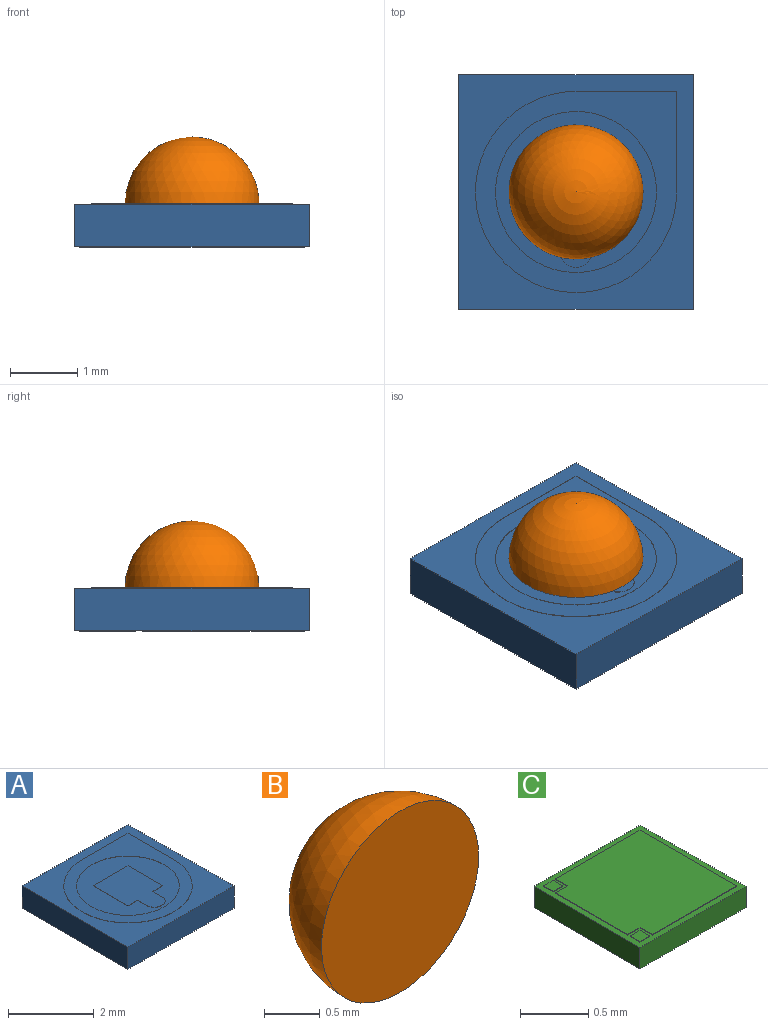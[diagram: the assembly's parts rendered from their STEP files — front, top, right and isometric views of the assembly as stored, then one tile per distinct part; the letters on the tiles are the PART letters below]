
ASSEMBLY  parts=3 mates=1
PART A: 31 faces, bbox 3.5x3.5x0.6 mm
  f0: plane 3.5x3.5mm, normal (0,0,-1), area 1.4mm2, adj f2,f3,f4,f5,f21,f22,f23,f24
  f1: plane 3.5x3.5mm, normal (0,0,1), area 4.7mm2, adj f2,f3,f4,f5,f6,f7,f9
  f2: plane 3.5x0.64mm, normal (0,-1,0), area 2.2mm2, adj f0,f1,f3,f5
  f3: plane 3.5x0.64mm, normal (1,0,0), area 2.2mm2, adj f0,f1,f2,f4
  f4: plane 3.5x0.64mm, normal (0,1,0), area 2.2mm2, adj f0,f1,f3,f5
  f5: plane 3.5x0.64mm, normal (-1,0,0), area 2.2mm2, adj f0,f1,f2,f4
  f6: plane 1.5x0.01mm, normal (1,0,0), area 0mm2, adj f1,f7,f9,f10
  f7: plane 1.5x0.01mm, normal (0,1,0), area 0mm2, adj f1,f6,f9,f10
  f8: cylinder r=1.2mm len=2.4mm, axis (0,0,-1), area 0mm2, adj f10,f11
  f9: cylinder r=1.5mm len=3mm, axis (0,0,-1), area 0mm2, adj f1,f6,f7,f10
  f10: plane 3x3mm, normal (0,0,1), area 3mm2, adj f6,f7,f8,f9
  f11: plane 2.4x2.4mm, normal (0,0,1), area 3mm2, adj f8,f12,f13,f14,f15,f16,f17,f18
  f12: plane 0.32x0.01mm, normal (0,-1,0), area 0mm2, adj f11,f13,f19,f20
  f13: plane 1.14x0.01mm, normal (1,0,0), area 0mm2, adj f11,f12,f14,f20
  f14: plane 1.14x0.01mm, normal (0,1,0), area 0mm2, adj f11,f13,f15,f20
  f15: plane 1.14x0.01mm, normal (-1,0,0), area 0mm2, adj f11,f14,f16,f20
  f16: plane 0.32x0.01mm, normal (0,-1,0), area 0mm2, adj f11,f15,f17,f20
  f17: plane 0.3x0.01mm, normal (-1,0,0), area 0mm2, adj f11,f16,f18,f20
  f18: cylinder r=0.25mm len=0.5mm, axis (0,0,-1), area 0mm2, adj f11,f17,f19,f20
  f19: plane 0.3x0.01mm, normal (1,0,0), area 0mm2, adj f11,f12,f18,f20
  f20: plane 1.69x1.14mm, normal (0,0,1), area 1.6mm2, adj f12,f13,f14,f15,f16,f17,f18,f19
  f21: plane 3.35x0.01mm, normal (0,-1,0), area 0mm2, adj f0,f22,f24,f25
  f22: plane 2.41x0.01mm, normal (-1,0,0), area 0mm2, adj f0,f21,f23,f25
  f23: plane 3.35x0.01mm, normal (0,1,0), area 0mm2, adj f0,f22,f24,f25
  f24: plane 2.41x0.01mm, normal (1,0,0), area 0mm2, adj f0,f21,f23,f25
  f25: plane 3.35x2.41mm, normal (0,0,-1), area 8.1mm2, adj f21,f22,f23,f24
  f26: plane 3.35x0.01mm, normal (0,1,0), area 0mm2, adj f0,f27,f29,f30
  f27: plane 0.84x0.01mm, normal (1,0,0), area 0mm2, adj f0,f26,f28,f30
  f28: plane 3.35x0.01mm, normal (0,-1,0), area 0mm2, adj f0,f27,f29,f30
  f29: plane 0.84x0.01mm, normal (-1,0,0), area 0mm2, adj f0,f26,f28,f30
  f30: plane 3.35x0.84mm, normal (0,0,-1), area 2.8mm2, adj f26,f27,f28,f29
PART B: 2 faces, bbox 2x1x2 mm
  f0: plane 2x2mm, normal (0,-1,0), area 3.1mm2, adj f1
  f1: sphere r=1mm, area 6.3mm2, adj f0
PART C: 25 faces, bbox 1.1x1.1x0.2 mm
  f0: plane 1.1x1.1mm, normal (0,0,1), area 0.2mm2, adj f1,f2,f3,f4,f6,f7,f8,f9
  f1: plane 1.1x0.19mm, normal (0,-1,0), area 0.2mm2, adj f0,f2,f4,f5
  f2: plane 1.1x0.19mm, normal (1,0,0), area 0.2mm2, adj f0,f1,f3,f5
  f3: plane 1.1x0.19mm, normal (0,1,0), area 0.2mm2, adj f0,f2,f4,f5
  f4: plane 1.1x0.19mm, normal (-1,0,0), area 0.2mm2, adj f0,f1,f3,f5
  f5: plane 1.1x1.1mm, normal (0,0,-1), area 1.2mm2, adj f1,f2,f3,f4
  f6: plane 0.88x0.01mm, normal (0,-1,0), area 0mm2, adj f0,f7,f13,f14
  f7: plane 1x0.01mm, normal (1,0,0), area 0mm2, adj f0,f6,f8,f14
  f8: plane 0.88x0.01mm, normal (0,1,0), area 0mm2, adj f0,f7,f9,f14
  f9: plane 0.13x0.01mm, normal (-1,0,0), area 0mm2, adj f0,f8,f10,f14
  f10: plane 0.13x0.01mm, normal (0,1,0), area 0mm2, adj f0,f9,f11,f14
  f11: plane 0.75x0.01mm, normal (-1,0,0), area 0mm2, adj f0,f10,f12,f14
  f12: plane 0.13x0.01mm, normal (0,-1,0), area 0mm2, adj f0,f11,f13,f14
  f13: plane 0.13x0.01mm, normal (-1,0,0), area 0mm2, adj f0,f6,f12,f14
  f14: plane 1x1mm, normal (0,0,1), area 1mm2, adj f6,f7,f8,f9,f10,f11,f12,f13
  f15: plane 0.1x0.01mm, normal (0,1,0), area 0mm2, adj f0,f16,f18,f19
  f16: plane 0.1x0.01mm, normal (-1,0,0), area 0mm2, adj f0,f15,f17,f19
  f17: plane 0.1x0.01mm, normal (0,-1,0), area 0mm2, adj f0,f16,f18,f19
  f18: plane 0.1x0.01mm, normal (1,0,0), area 0mm2, adj f0,f15,f17,f19
  f19: plane 0.1x0.1mm, normal (0,0,1), area 0mm2, adj f15,f16,f17,f18
  f20: plane 0.1x0.01mm, normal (1,0,0), area 0mm2, adj f0,f21,f23,f24
  f21: plane 0.1x0.01mm, normal (0,1,0), area 0mm2, adj f0,f20,f22,f24
  f22: plane 0.1x0.01mm, normal (-1,0,0), area 0mm2, adj f0,f21,f23,f24
  f23: plane 0.1x0.01mm, normal (0,-1,0), area 0mm2, adj f0,f20,f22,f24
  f24: plane 0.1x0.1mm, normal (0,0,1), area 0mm2, adj f20,f21,f22,f23
PLACE A t=(-0.56,-0.17,-0.09)mm
PLACE B rot(axis=(1,0,0),90deg) t=(-0.56,-0.17,0.54)mm
PLACE C rot(axis=(0,0,1),0deg) t=(-0.56,-0.17,0.55)mm
MATE parallel C.f5 <-> A.f20  axis (0,0,-1) through (-0.56,-0.17,0.55)mm
